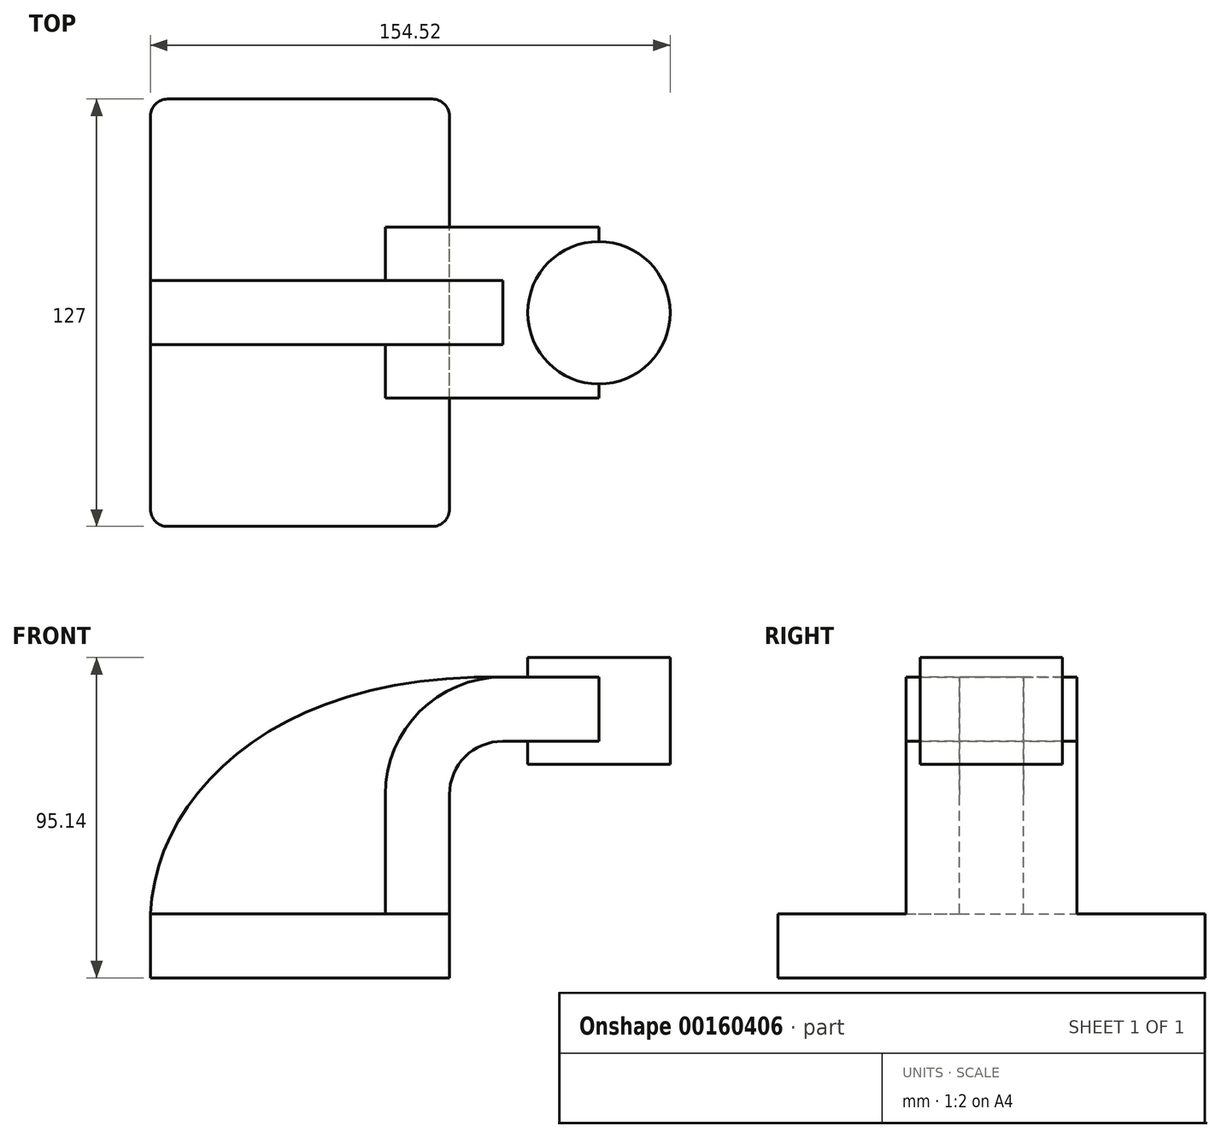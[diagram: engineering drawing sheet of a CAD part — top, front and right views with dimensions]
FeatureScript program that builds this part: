
annotation { "Feature Type Name" : "Feature", "Feature Type Description" : "" }
export const myFeature = defineFeature(function(context is Context, id is Id, definition is map)
    precondition{}
    {
        {
            var Q0;
            Q0=qCreatedBy(makeId("Front.planeOp"),FACE);
            var sketch = newSketch(context, id + "F0", { "sketchPlane" : qUnion([Q0])});
            skLineSegment(sketch, "E0.bottom", {"start": v(44.45, 9.53) * mm, "end": v(-44.45, 9.53) * mm});
            skLineSegment(sketch, "E0.top", {"start": v(44.45, -9.53) * mm, "end": v(-44.45, -9.53) * mm});
            skLineSegment(sketch, "E0.left", {"start": v(44.45, 9.53) * mm, "end": v(44.45, -9.53) * mm});
            skLineSegment(sketch, "E0.right", {"start": v(-44.45, 9.53) * mm, "end": v(-44.45, -9.53) * mm});
            skPoint(sketch, "E0.middle", {"position": v(0, 0) * mm});
            skLineSegment(sketch, "E1.bottom", {"start": v(110.07, 85.61) * mm, "end": v(67.73, 85.61) * mm});
            skLineSegment(sketch, "E1.top", {"start": v(110.07, 53.86) * mm, "end": v(67.73, 53.86) * mm});
            skLineSegment(sketch, "E1.left", {"start": v(110.07, 85.61) * mm, "end": v(110.07, 53.86) * mm});
            skLineSegment(sketch, "E1.right", {"start": v(67.73, 85.61) * mm, "end": v(67.73, 53.86) * mm});
            skPoint(sketch, "E1.middle", {"position": v(88.9, 69.74) * mm});
            skLineSegment(sketch, "E2", {"start": v(44.45, 9.53) * mm, "end": v(44.45, 44.9) * mm});
            skLineSegment(sketch, "E3", {"start": v(60.32, 60.78) * mm, "end": v(88.9, 60.78) * mm});
            skPoint(sketch, "E4.visualSharp", {"position": v(44.45, 60.78) * mm});
            skArc(sketch, "E4.filletArc", {"start": v(60.32, 60.78) * mm, "mid": v(49.1, 56.13) * mm, "end": v(44.45, 44.9) * mm});
            skLineSegment(sketch, "E5.0", {"start": v(60.32, 79.83) * mm, "end": v(88.9, 79.83) * mm});
            skArc(sketch, "E5.1", {"start": v(60.32, 79.83) * mm, "mid": v(35.63, 69.6) * mm, "end": v(25.4, 44.9) * mm});
            skLineSegment(sketch, "E5.2", {"start": v(25.4, 9.53) * mm, "end": v(25.4, 44.9) * mm});
            skLineSegment(sketch, "E6", {"start": v(88.9, 85.61) * mm, "end": v(88.9, 53.86) * mm});
            skPoint(sketch, "E7", {"position": v(44.45, 0) * mm});
            skFitSpline(sketch, "E8", {"points": [v(-44.45, 9.52) * mm, v(60.32, 79.83) * mm], "startDerivative": vector(5.12, 108.22) * mm, "endDerivative": vector(200.8, -4.17) * mm});
            skSolve(sketch);
        }
        {
            var Q0;
            Q0=makeQuery(id+"F0.imprint","IMPRINT",FACE,{"disambiguationData":[TD([[makeQuery(id+"F0.imprint","IMPRINT",EDGE,{"derivedFrom":sQuery(id+"F0.wireOp",EDGE,"E0.top")}),-1.0]])]});
            extrude(context, id + "F1", {"entities" : qUnion([Q0]), "endBound" : BoundingType.SYMMETRIC, "depth" : 127 * mm});
        }
        {
            var Q0;
            {var subQ4=sQuery(id+"F0.wireOp",EDGE,"E2");Q0=makeQuery(id+"F0.imprint","IMPRINT",FACE,{"disambiguationData":[TD([[makeQuery(id+"F0.imprint","IMPRINT",EDGE,{"derivedFrom":subQ4}),1.0]])]});}
            var Q1;
            {var subQ0=sQuery(id+"F0.wireOp",EDGE,"E5.0");var subQ1=sQuery(id+"F0.wireOp",EDGE,"E1.right");var subQ2=makeQuery(id+"F0.imprint","INTERSECT",VERTEX,{"derivedFrom":[subQ1,subQ0]});Q1=makeQuery(id+"F0.imprint","IMPRINT",FACE,{"disambiguationData":[TD([[makeQuery(id+"F0.imprint","IMPRINT",EDGE,{"disambiguationData":[TD([[subQ2,-1.0]])],"derivedFrom":subQ1}),1.0]])]});}
            extrude(context, id + "F2", {"entities" : qUnion([Q0, Q1]), "operationType" : NewBodyOperationType.ADD, "endBound" : BoundingType.SYMMETRIC, "depth" : 50.8 * mm});
        }
        {
            var Q0;
            Q0=makeQuery(id+"F0.imprint","IMPRINT",FACE,{"disambiguationData":[TD([[makeQuery(id+"F0.imprint","IMPRINT",EDGE,{"derivedFrom":sQuery(id+"F0.wireOp",EDGE,"E5.1")}),-1.0]])]});
            extrude(context, id + "F3", {"entities" : qUnion([Q0]), "operationType" : NewBodyOperationType.ADD, "endBound" : BoundingType.SYMMETRIC, "depth" : 19.05 * mm});
        }
        {
            var Q0;
            {var subQ0=sQuery(id+"F0.wireOp",EDGE,"E1.left");Q0=makeQuery(id+"F0.imprint","IMPRINT",FACE,{"disambiguationData":[TD([[makeQuery(id+"F0.imprint","IMPRINT",EDGE,{"derivedFrom":subQ0}),-1.0]])]});}
            var Q1;
            Q1=sQuery(id+"F0.wireOp",EDGE,"E6");
            revolve(context, id + "F4", {"operationType" : NewBodyOperationType.ADD, "entities" : qUnion([Q0]), "axis" : qUnion([Q1]), "revolveType" : RevolveType.FULL});
        }
        {
            var Q0;
            Q0=makeQuery(id+"F1.opExtrude","CAP_EDGE",EDGE,{"disambiguationData":[OSD([sQuery(id+"F0.wireOp",EDGE,"E0.right")])],"isStart":false});
            var Q1;
            Q1=makeQuery(id+"F1.opExtrude","CAP_EDGE",EDGE,{"disambiguationData":[OSD([sQuery(id+"F0.wireOp",EDGE,"E0.left")])],"isStart":false});
            var Q2;
            Q2=makeQuery(id+"F1.opExtrude","CAP_EDGE",EDGE,{"disambiguationData":[OSD([sQuery(id+"F0.wireOp",EDGE,"E0.left")])],"isStart":true});
            var Q3;
            Q3=makeQuery(id+"F1.opExtrude","CAP_EDGE",EDGE,{"disambiguationData":[OSD([sQuery(id+"F0.wireOp",EDGE,"E0.right")])],"isStart":true});
            fillet(context, id + "F5", {"entities" : qUnion([Q0, Q1, Q2, Q3]), "radius" : 5.08 * mm, "tangentPropagation" : true, "allowEdgeOverflow" : false});
        }
    });
